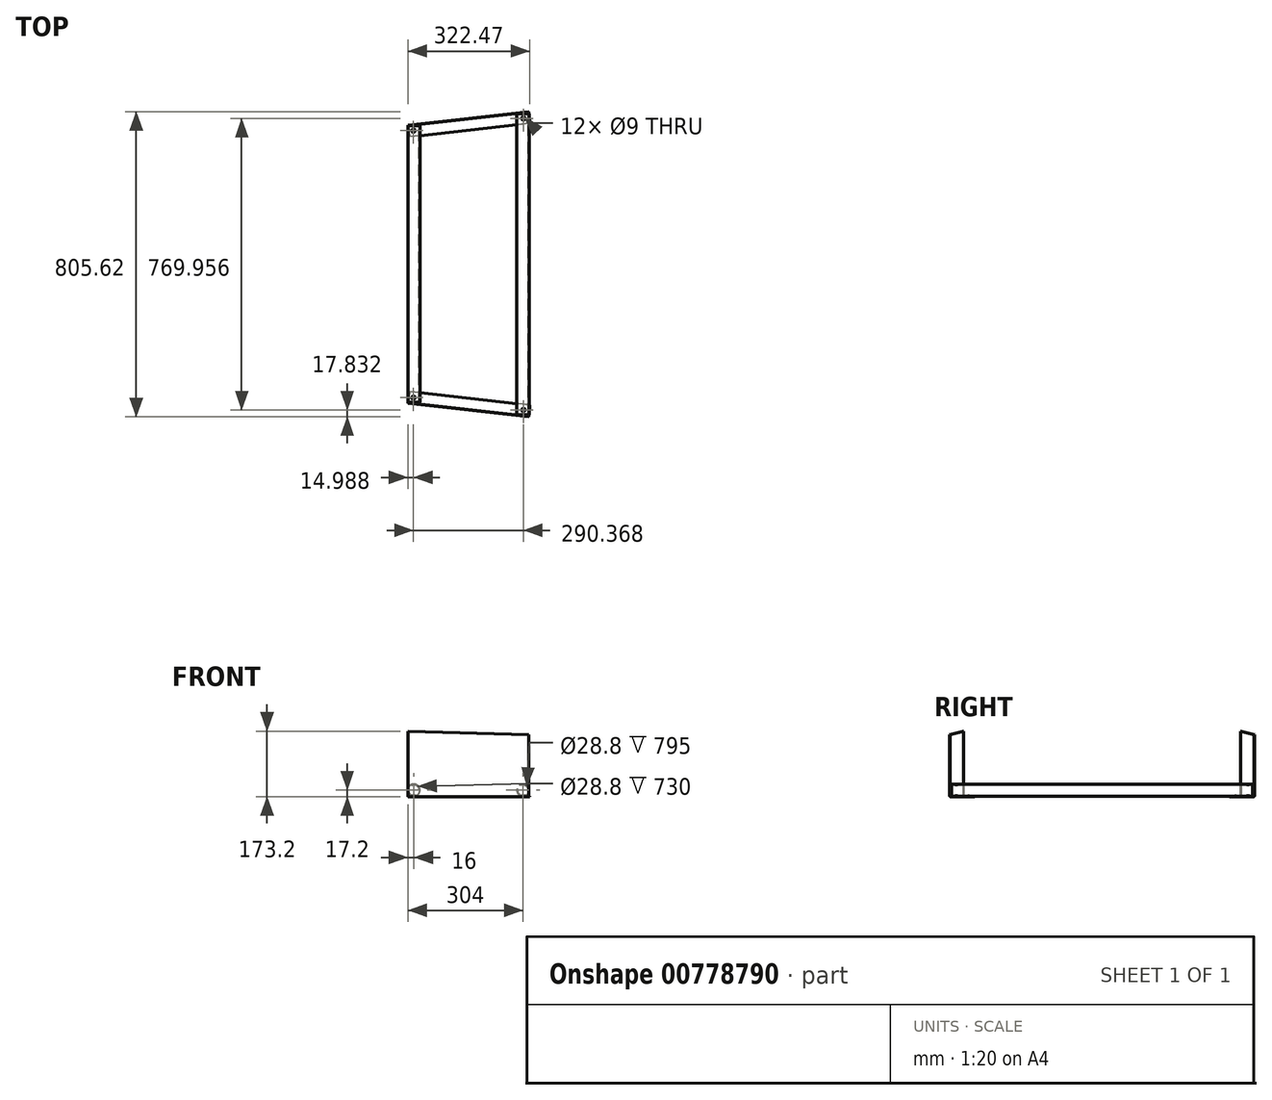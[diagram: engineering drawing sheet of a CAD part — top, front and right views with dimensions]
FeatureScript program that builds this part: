
annotation { "Feature Type Name" : "Feature", "Feature Type Description" : "" }
export const myFeature = defineFeature(function(context is Context, id is Id, definition is map)
    precondition{}
    {
        {
            var Q0;
            Q0=qCreatedBy(makeId("Front.planeOp"),FACE);
            var sketch = newSketch(context, id + "F0", { "sketchPlane" : qUnion([Q0])});
            skCircle(sketch, "E0", {"center": v(-144, 0) * mm, "radius": 16 * mm});
            skCircle(sketch, "E1.0", {"center": v(-144, 0) * mm, "radius": 14.4 * mm});
            skSolve(sketch);
        }
        {
            var Q0;
            Q0 = qSketchRegion(id + "F0", true);
            extrude(context, id + "F1", {"entities" : qUnion([Q0]), "depth" : 730 * mm, "offsetDistance" : 25 * mm, "symmetric" : true});
        }
        {
            var Q0;
            Q0=qCreatedBy(makeId("Front.planeOp"),FACE);
            var sketch = newSketch(context, id + "F2", { "sketchPlane" : qUnion([Q0])});
            skCircle(sketch, "E2", {"center": v(144, 0) * mm, "radius": 16 * mm});
            skCircle(sketch, "E3.0", {"center": v(144, 0) * mm, "radius": 14.4 * mm});
            skSolve(sketch);
        }
        {
            var Q0;
            Q0 = qSketchRegion(id + "F2", true);
            extrude(context, id + "F3", {"entities" : qUnion([Q0]), "depth" : 795 * mm, "offsetDistance" : 25 * mm, "symmetric" : true});
        }
        {
            var Q0;
            Q0=qCreatedBy(makeId("Top.planeOp"),FACE);
            var sketch = newSketch(context, id + "F4", { "sketchPlane" : qUnion([Q0])});
            skLineSegment(sketch, "E4", {"start": v(-158.88, -366) * mm, "end": v(159.13, -401.61) * mm});
            skLineSegment(sketch, "E5.0", {"start": v(-159.01, -367.2) * mm, "end": v(159, -402.8) * mm});
            skLineSegment(sketch, "E6", {"start": v(159.13, -401.61) * mm, "end": v(159, -402.8) * mm});
            skLineSegment(sketch, "E7", {"start": v(-158.88, -366) * mm, "end": v(-159.01, -367.2) * mm});
            skSolve(sketch);
        }
        {
            var Q0;
            Q0 = qSketchRegion(id + "F4", true);
            extrude(context, id + "F5", {"entities" : qUnion([Q0]), "depth" : 156 * mm, "offsetDistance" : 25 * mm});
        }
        {
            var Q0;
            Q0=makeQuery(id+"F5.opExtrude","SWEPT_FACE",FACE,{"disambiguationData":[OSD([sQuery(id+"F4.wireOp",EDGE,"E7")])]});
            var sketch = newSketch(context, id + "F6", { "sketchPlane" : qUnion([Q0])});
            skLineSegment(sketch, "E8", {"start": v(381.4, 0) * mm, "end": v(381.4, -14) * mm});
            skLineSegment(sketch, "E9", {"start": v(379.4, -16) * mm, "end": v(351.4, -16) * mm});
            skLineSegment(sketch, "E10", {"start": v(351.4, -16) * mm, "end": v(351.4, -17.2) * mm});
            skLineSegment(sketch, "E11", {"start": v(351.4, -17.2) * mm, "end": v(379.6, -17.2) * mm});
            skLineSegment(sketch, "E12", {"start": v(382.6, -14.2) * mm, "end": v(382.6, 0) * mm});
            skPoint(sketch, "E13.visualSharp", {"position": v(381.4, -16) * mm});
            skArc(sketch, "E13.filletArc", {"start": v(379.4, -16) * mm, "mid": v(380.82, -15.41) * mm, "end": v(381.4, -14) * mm});
            skPoint(sketch, "E14.visualSharp", {"position": v(382.6, -17.2) * mm});
            skArc(sketch, "E14.filletArc", {"start": v(379.6, -17.2) * mm, "mid": v(381.73, -16.32) * mm, "end": v(382.6, -14.2) * mm});
            skLineSegment(sketch, "E15", {"start": v(381.4, 0) * mm, "end": v(382.6, 0) * mm});
            skSolve(sketch);
        }
        {
            var Q0;
            Q0 = qSketchRegion(id + "F6", true);
            extrude(context, id + "F7", {"entities" : qUnion([Q0]), "operationType" : NewBodyOperationType.ADD, "oppositeDirection" : true, "depth" : 320 * mm, "offsetDistance" : 25 * mm});
        }
        {
            var Q0;
            Q0=makeQuery(id+"F7.boolean.opBoolean","MERGE",FACE,{"derivedFrom":[makeQuery(id+"F5.opExtrude","SWEPT_FACE",FACE,{"disambiguationData":[OSD([sQuery(id+"F4.wireOp",EDGE,"E5.0")])]}),makeQuery(id+"F7.opExtrude","SWEPT_FACE",FACE,{"disambiguationData":[OSD([sQuery(id+"F6.wireOp",EDGE,"E12")])]})]});
            var sketch = newSketch(context, id + "F8", { "sketchPlane" : qUnion([Q0])});
            skLineSegment(sketch, "E16", {"start": v(-117.16, 156) * mm, "end": v(202.84, 146) * mm});
            skLineSegment(sketch, "E17", {"start": v(202.84, 146) * mm, "end": v(202.84, 156) * mm});
            skLineSegment(sketch, "E18", {"start": v(202.84, 156) * mm, "end": v(-117.16, 156) * mm});
            skSolve(sketch);
        }
        {
            var Q0;
            Q0 = qSketchRegion(id + "F8", true);
            extrude(context, id + "F9", {"entities" : qUnion([Q0]), "operationType" : NewBodyOperationType.REMOVE, "endBound" : BoundingType.UP_TO_NEXT, "oppositeDirection" : true, "depth" : 25 * mm, "offsetDistance" : 25 * mm});
        }
        {
            var Q0;
            Q0=makeQuery(id+"F5.opExtrude","SWEPT_BODY",BODY,{"disambiguationData":[OSD([sQuery(id+"F4.wireOp",EDGE,"E4"),sQuery(id+"F4.wireOp",EDGE,"E5.0"),sQuery(id+"F4.wireOp",EDGE,"E6"),sQuery(id+"F4.wireOp",EDGE,"E7")])]});
            var Q1;
            Q1=qCreatedBy(makeId("Front.planeOp"),FACE);
            mirror(context, id + "F10", {"entities" : qUnion([Q0]), "mirrorPlane" : qUnion([Q1])});
        }
        {
            var Q0;
            Q0=qCreatedBy(makeId("Top.planeOp"),FACE);
            var sketch = newSketch(context, id + "F11", { "sketchPlane" : qUnion([Q0])});
            skCircle(sketch, "E19", {"center": v(-145.01, -352.46) * mm, "radius": 4.5 * mm});
            skCircle(sketch, "E20", {"center": v(145.36, -384.98) * mm, "radius": 4.5 * mm});
            skCircle(sketch, "E21", {"center": v(145.36, 384.98) * mm, "radius": 4.5 * mm});
            skCircle(sketch, "E22", {"center": v(-144.88, 352.47) * mm, "radius": 4.5 * mm});
            skSolve(sketch);
        }
        {
            var Q0;
            Q0 = qSketchRegion(id + "F11", true);
            extrude(context, id + "F12", {"entities" : qUnion([Q0]), "operationType" : NewBodyOperationType.REMOVE, "depth" : 36 * mm, "offsetDistance" : 25 * mm, "symmetric" : true});
        }
    });
